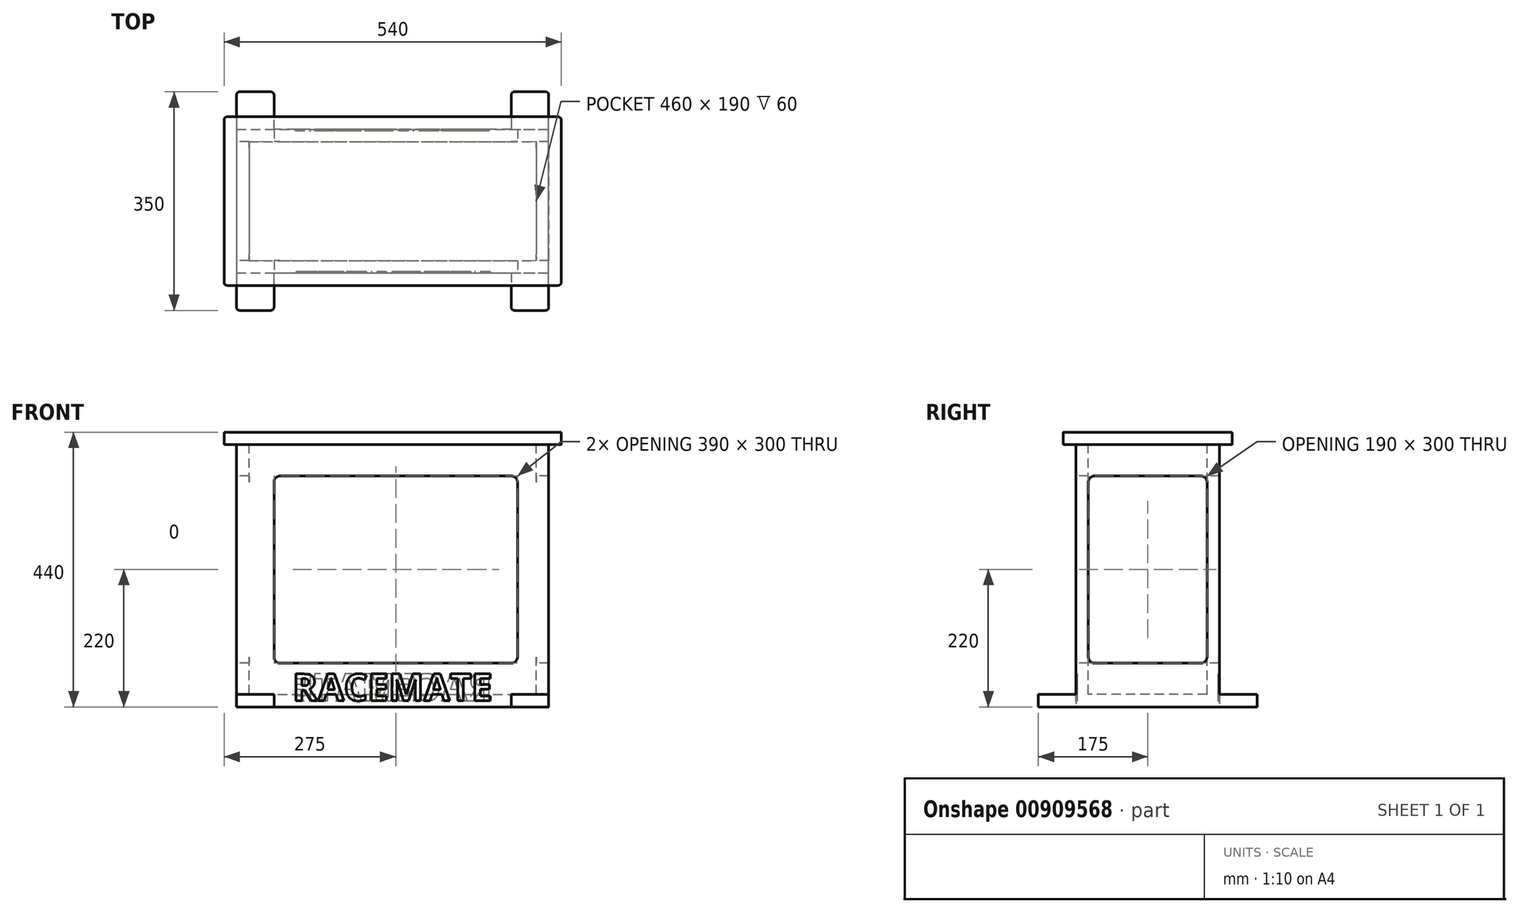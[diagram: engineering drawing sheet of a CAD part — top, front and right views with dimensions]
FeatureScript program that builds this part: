
annotation { "Feature Type Name" : "Feature", "Feature Type Description" : "" }
export const myFeature = defineFeature(function(context is Context, id is Id, definition is map)
    precondition{}
    {
        {
            var Q0;
            Q0=qCreatedBy(makeId("Top.planeOp"),FACE);
            var sketch = newSketch(context, id + "F0", { "sketchPlane" : qUnion([Q0])});
            skLineSegment(sketch, "E0", {"start": v(0, 0) * mm, "end": v(60, 0) * mm});
            skLineSegment(sketch, "E1", {"start": v(60, 0) * mm, "end": v(60, 60) * mm});
            skLineSegment(sketch, "E2", {"start": v(60, 60) * mm, "end": v(440, 60) * mm});
            skLineSegment(sketch, "E3", {"start": v(440, 60) * mm, "end": v(440, 0) * mm});
            skLineSegment(sketch, "E4", {"start": v(440, 0) * mm, "end": v(500, 0) * mm});
            skLineSegment(sketch, "E5", {"start": v(500, 0) * mm, "end": v(500, 350) * mm});
            skLineSegment(sketch, "E6", {"start": v(500, 350) * mm, "end": v(440, 350) * mm});
            skLineSegment(sketch, "E7", {"start": v(440, 350) * mm, "end": v(440, 290) * mm});
            skLineSegment(sketch, "E8", {"start": v(440, 290) * mm, "end": v(60, 290) * mm});
            skLineSegment(sketch, "E9", {"start": v(60, 290) * mm, "end": v(60, 350) * mm});
            skLineSegment(sketch, "E10", {"start": v(60, 350) * mm, "end": v(0, 350) * mm});
            skLineSegment(sketch, "E11", {"start": v(0, 350) * mm, "end": v(0, 0) * mm});
            skSolve(sketch);
        }
        {
            var Q0;
            Q0=makeQuery(id+"F0.imprint","IMPRINT",FACE,{"disambiguationData":[TD([[makeQuery(id+"F0.imprint","IMPRINT",EDGE,{"derivedFrom":sQuery(id+"F0.wireOp",EDGE,"E0")}),1.0]])]});
            var Q1;
            Q1 = qSketchRegion(id + "F2", true);
            extrude(context, id + "F1", {"entities" : qUnion([Q0, Q1]), "depth" : 20 * mm, "offsetDistance" : 25 * mm});
        }
        {
            var Q0;
            Q0=makeQuery(id+"F1.opExtrude","CAP_FACE",FACE,{"disambiguationData":[OSD([sQuery(id+"F0.wireOp",EDGE,"E0"),sQuery(id+"F0.wireOp",EDGE,"E1"),sQuery(id+"F0.wireOp",EDGE,"E2"),sQuery(id+"F0.wireOp",EDGE,"E3"),sQuery(id+"F0.wireOp",EDGE,"E4"),sQuery(id+"F0.wireOp",EDGE,"E5"),sQuery(id+"F0.wireOp",EDGE,"E6"),sQuery(id+"F0.wireOp",EDGE,"E7"),sQuery(id+"F0.wireOp",EDGE,"E8"),sQuery(id+"F0.wireOp",EDGE,"E9"),sQuery(id+"F0.wireOp",EDGE,"E10"),sQuery(id+"F0.wireOp",EDGE,"E11")])],"isStart":false});
            var sketch = newSketch(context, id + "F2", { "sketchPlane" : qUnion([Q0])});
            skLineSegment(sketch, "E12.bottom", {"start": v(0, 290) * mm, "end": v(500, 290) * mm});
            skLineSegment(sketch, "E12.top", {"start": v(0, 60) * mm, "end": v(500, 60) * mm});
            skLineSegment(sketch, "E12.left", {"start": v(0, 290) * mm, "end": v(0, 60) * mm});
            skLineSegment(sketch, "E12.right", {"start": v(500, 290) * mm, "end": v(500, 60) * mm});
            skSolve(sketch);
        }
        {
            var Q0;
            Q0 = qSketchRegion(id + "F2", true);
            var Q1;
            Q1 = qSketchRegion(id + "F4", true);
            extrude(context, id + "F3", {"entities" : qUnion([Q0, Q1]), "operationType" : NewBodyOperationType.ADD, "depth" : 400 * mm, "offsetDistance" : 25 * mm});
        }
        {
            var Q0;
            Q0=makeQuery(id+"F3.opExtrude","CAP_FACE",FACE,{"disambiguationData":[OSD([sQuery(id+"F2.wireOp",EDGE,"E12.bottom"),sQuery(id+"F2.wireOp",EDGE,"E12.top"),sQuery(id+"F2.wireOp",EDGE,"E12.left"),sQuery(id+"F2.wireOp",EDGE,"E12.right")])],"isStart":false});
            var sketch = newSketch(context, id + "F4", { "sketchPlane" : qUnion([Q0])});
            skLineSegment(sketch, "E13.bottom", {"start": v(20, 270) * mm, "end": v(480, 270) * mm});
            skLineSegment(sketch, "E13.top", {"start": v(20, 80) * mm, "end": v(480, 80) * mm});
            skLineSegment(sketch, "E13.left", {"start": v(20, 270) * mm, "end": v(20, 80) * mm});
            skLineSegment(sketch, "E13.right", {"start": v(480, 270) * mm, "end": v(480, 80) * mm});
            skSolve(sketch);
        }
        {
            var Q0;
            Q0 = qSketchRegion(id + "F4", true);
            extrude(context, id + "F5", {"entities" : qUnion([Q0]), "operationType" : NewBodyOperationType.REMOVE, "oppositeDirection" : true, "depth" : 400 * mm, "offsetDistance" : 25 * mm});
        }
        {
            var Q0;
            Q0=makeQuery(id+"F3.boolean.opBoolean","MERGE",FACE,{"derivedFrom":[makeQuery(id+"F1.opExtrude","SWEPT_FACE",FACE,{"disambiguationData":[OSD([sQuery(id+"F0.wireOp",EDGE,"E11")])]}),makeQuery(id+"F3.opExtrude","SWEPT_FACE",FACE,{"disambiguationData":[OSD([sQuery(id+"F2.wireOp",EDGE,"E12.left")])]})]});
            var sketch = newSketch(context, id + "F6", { "sketchPlane" : qUnion([Q0])});
            skLineSegment(sketch, "E14.bottom", {"start": v(-270, 370) * mm, "end": v(-80, 370) * mm});
            skLineSegment(sketch, "E14.top", {"start": v(-270, 70) * mm, "end": v(-80, 70) * mm});
            skLineSegment(sketch, "E14.left", {"start": v(-270, 370) * mm, "end": v(-270, 70) * mm});
            skLineSegment(sketch, "E14.right", {"start": v(-80, 370) * mm, "end": v(-80, 70) * mm});
            skSolve(sketch);
        }
        {
            var Q0;
            Q0 = qSketchRegion(id + "F6", true);
            extrude(context, id + "F7", {"entities" : qUnion([Q0]), "operationType" : NewBodyOperationType.REMOVE, "endBound" : BoundingType.THROUGH_ALL, "oppositeDirection" : true, "depth" : 25 * mm, "offsetDistance" : 25 * mm});
        }
        {
            var Q0;
            Q0=makeQuery(id+"F3.boolean.opBoolean","MERGE",FACE,{"derivedFrom":[makeQuery(id+"F1.opExtrude","SWEPT_FACE",FACE,{"disambiguationData":[OSD([sQuery(id+"F0.wireOp",EDGE,"E2")])]}),makeQuery(id+"F3.opExtrude","SWEPT_FACE",FACE,{"disambiguationData":[OSD([sQuery(id+"F2.wireOp",EDGE,"E12.top")])]})]});
            var sketch = newSketch(context, id + "F8", { "sketchPlane" : qUnion([Q0])});
            skLineSegment(sketch, "E15.bottom", {"start": v(60, 370) * mm, "end": v(450, 370) * mm});
            skLineSegment(sketch, "E15.top", {"start": v(60, 70) * mm, "end": v(450, 70) * mm});
            skLineSegment(sketch, "E15.left", {"start": v(60, 370) * mm, "end": v(60, 70) * mm});
            skLineSegment(sketch, "E15.right", {"start": v(450, 370) * mm, "end": v(450, 70) * mm});
            skSolve(sketch);
        }
        {
            var Q0;
            Q0 = qSketchRegion(id + "F8", true);
            extrude(context, id + "F9", {"entities" : qUnion([Q0]), "operationType" : NewBodyOperationType.REMOVE, "endBound" : BoundingType.THROUGH_ALL, "oppositeDirection" : true, "depth" : 25 * mm, "offsetDistance" : 25 * mm});
        }
        {
            var Q0;
            Q0=makeQuery(id+"F3.opExtrude","CAP_FACE",FACE,{"disambiguationData":[OSD([sQuery(id+"F2.wireOp",EDGE,"E12.bottom"),sQuery(id+"F2.wireOp",EDGE,"E12.top"),sQuery(id+"F2.wireOp",EDGE,"E12.left"),sQuery(id+"F2.wireOp",EDGE,"E12.right")])],"isStart":false});
            var sketch = newSketch(context, id + "F10", { "sketchPlane" : qUnion([Q0])});
            skLineSegment(sketch, "E16", {"start": v(-20, 310) * mm, "end": v(-20, 40) * mm});
            skLineSegment(sketch, "E17", {"start": v(-20, 40) * mm, "end": v(520, 40) * mm});
            skLineSegment(sketch, "E18", {"start": v(520, 40) * mm, "end": v(520, 310) * mm});
            skLineSegment(sketch, "E19", {"start": v(520, 310) * mm, "end": v(-20, 310) * mm});
            skSolve(sketch);
        }
        {
            var Q0;
            Q0 = qSketchRegion(id + "F10", true);
            extrude(context, id + "F11", {"entities" : qUnion([Q0]), "operationType" : NewBodyOperationType.ADD, "surfaceOperationType" : NewSurfaceOperationType.ADD, "depth" : 20 * mm, "offsetDistance" : 25 * mm});
        }
        {
            var Q0;
            Q0=makeQuery(id+"F1.opExtrude","SWEPT_EDGE",EDGE,{"disambiguationData":[OSD([sQuery(id+"F0.wireOp",EDGE,"E0"),sQuery(id+"F0.wireOp",EDGE,"E11")])]});
            var Q1;
            Q1=makeQuery(id+"F1.opExtrude","SWEPT_EDGE",EDGE,{"disambiguationData":[OSD([sQuery(id+"F0.wireOp",EDGE,"E0"),sQuery(id+"F0.wireOp",EDGE,"E1")])]});
            var Q2;
            Q2=makeQuery(id+"F1.opExtrude","SWEPT_EDGE",EDGE,{"disambiguationData":[OSD([sQuery(id+"F0.wireOp",EDGE,"E10"),sQuery(id+"F0.wireOp",EDGE,"E11")])]});
            var Q3;
            Q3=makeQuery(id+"F1.opExtrude","SWEPT_EDGE",EDGE,{"disambiguationData":[OSD([sQuery(id+"F0.wireOp",EDGE,"E4"),sQuery(id+"F0.wireOp",EDGE,"E5")])]});
            var Q4;
            Q4=makeQuery(id+"F1.opExtrude","SWEPT_EDGE",EDGE,{"disambiguationData":[OSD([sQuery(id+"F0.wireOp",EDGE,"E3"),sQuery(id+"F0.wireOp",EDGE,"E4")])]});
            var Q5;
            Q5=makeQuery(id+"F1.opExtrude","SWEPT_EDGE",EDGE,{"disambiguationData":[OSD([sQuery(id+"F0.wireOp",EDGE,"E9"),sQuery(id+"F0.wireOp",EDGE,"E10")])]});
            var Q6;
            Q6=makeQuery(id+"F1.opExtrude","SWEPT_EDGE",EDGE,{"disambiguationData":[OSD([sQuery(id+"F0.wireOp",EDGE,"E5"),sQuery(id+"F0.wireOp",EDGE,"E6")])]});
            var Q7;
            Q7=makeQuery(id+"F1.opExtrude","SWEPT_EDGE",EDGE,{"disambiguationData":[OSD([sQuery(id+"F0.wireOp",EDGE,"E6"),sQuery(id+"F0.wireOp",EDGE,"E7")])]});
            fillet(context, id + "F12", {"entities" : qUnion([Q0, Q1, Q2, Q3, Q4, Q5, Q6, Q7]), "radius" : 5 * mm, "tangentPropagation" : true, "allowEdgeOverflow" : false});
        }
        {
            var Q0;
            Q0=makeQuery(id+"F11.opExtrude","SWEPT_EDGE",EDGE,{"disambiguationData":[OSD([sQuery(id+"F10.wireOp",EDGE,"E18"),sQuery(id+"F10.wireOp",EDGE,"E19")])]});
            var Q1;
            Q1=makeQuery(id+"F11.opExtrude","SWEPT_EDGE",EDGE,{"disambiguationData":[OSD([sQuery(id+"F10.wireOp",EDGE,"E16"),sQuery(id+"F10.wireOp",EDGE,"E19")])]});
            var Q2;
            Q2=makeQuery(id+"F11.opExtrude","SWEPT_EDGE",EDGE,{"disambiguationData":[OSD([sQuery(id+"F10.wireOp",EDGE,"E16"),sQuery(id+"F10.wireOp",EDGE,"E17")])]});
            var Q3;
            Q3=makeQuery(id+"F11.opExtrude","SWEPT_EDGE",EDGE,{"disambiguationData":[OSD([sQuery(id+"F10.wireOp",EDGE,"E17"),sQuery(id+"F10.wireOp",EDGE,"E18")])]});
            fillet(context, id + "F13", {"entities" : qUnion([Q0, Q1, Q2, Q3]), "radius" : 5 * mm, "tangentPropagation" : true, "allowEdgeOverflow" : false});
        }
        {
            var Q0;
            {var subQ0=sQuery(id+"F8.wireOp",EDGE,"E15.top");var subQ1=sQuery(id+"F8.wireOp",EDGE,"E15.left");Q0=makeQuery(id+"F9.boolean.opBoolean","COPY",EDGE,{"disambiguationData":[TD([makeQuery(id+"F1.opExtrude","SWEPT_FACE",FACE,{"disambiguationData":[OSD([sQuery(id+"F0.wireOp",EDGE,"E2")])]})])],"derivedFrom":makeQuery(id+"F9.opExtrude","SWEPT_EDGE",EDGE,{"disambiguationData":[OSD([subQ0,subQ1])]})});}
            var Q1;
            {var subQ0=sQuery(id+"F8.wireOp",EDGE,"E15.top");var subQ1=sQuery(id+"F8.wireOp",EDGE,"E15.left");Q1=makeQuery(id+"F9.boolean.opBoolean","COPY",EDGE,{"disambiguationData":[TD([makeQuery(id+"F1.opExtrude","SWEPT_FACE",FACE,{"disambiguationData":[OSD([sQuery(id+"F0.wireOp",EDGE,"E8")])]})])],"derivedFrom":makeQuery(id+"F9.opExtrude","SWEPT_EDGE",EDGE,{"disambiguationData":[OSD([subQ0,subQ1])]})});}
            var Q2;
            {var subQ0=sQuery(id+"F6.wireOp",EDGE,"E14.top");var subQ1=sQuery(id+"F6.wireOp",EDGE,"E14.left");Q2=makeQuery(id+"F7.boolean.opBoolean","COPY",EDGE,{"disambiguationData":[TD([makeQuery(id+"F1.opExtrude","SWEPT_FACE",FACE,{"disambiguationData":[OSD([sQuery(id+"F0.wireOp",EDGE,"E11")])]})])],"derivedFrom":makeQuery(id+"F7.opExtrude","SWEPT_EDGE",EDGE,{"disambiguationData":[OSD([subQ0,subQ1])]})});}
            var Q3;
            {var subQ0=sQuery(id+"F6.wireOp",EDGE,"E14.top");var subQ1=sQuery(id+"F6.wireOp",EDGE,"E14.left");Q3=makeQuery(id+"F7.boolean.opBoolean","COPY",EDGE,{"disambiguationData":[TD([makeQuery(id+"F1.opExtrude","SWEPT_FACE",FACE,{"disambiguationData":[OSD([sQuery(id+"F0.wireOp",EDGE,"E5")])]})])],"derivedFrom":makeQuery(id+"F7.opExtrude","SWEPT_EDGE",EDGE,{"disambiguationData":[OSD([subQ0,subQ1])]})});}
            var Q4;
            {var subQ0=sQuery(id+"F8.wireOp",EDGE,"E15.top");var subQ1=sQuery(id+"F8.wireOp",EDGE,"E15.right");Q4=makeQuery(id+"F9.boolean.opBoolean","COPY",EDGE,{"disambiguationData":[TD([makeQuery(id+"F1.opExtrude","SWEPT_FACE",FACE,{"disambiguationData":[OSD([sQuery(id+"F0.wireOp",EDGE,"E2")])]})])],"derivedFrom":makeQuery(id+"F9.opExtrude","SWEPT_EDGE",EDGE,{"disambiguationData":[OSD([subQ0,subQ1])]})});}
            var Q5;
            {var subQ0=sQuery(id+"F6.wireOp",EDGE,"E14.top");var subQ1=sQuery(id+"F6.wireOp",EDGE,"E14.right");Q5=makeQuery(id+"F7.boolean.opBoolean","COPY",EDGE,{"disambiguationData":[TD([makeQuery(id+"F1.opExtrude","SWEPT_FACE",FACE,{"disambiguationData":[OSD([sQuery(id+"F0.wireOp",EDGE,"E5")])]})])],"derivedFrom":makeQuery(id+"F7.opExtrude","SWEPT_EDGE",EDGE,{"disambiguationData":[OSD([subQ0,subQ1])]})});}
            var Q6;
            {var subQ0=sQuery(id+"F8.wireOp",EDGE,"E15.top");var subQ1=sQuery(id+"F8.wireOp",EDGE,"E15.right");Q6=makeQuery(id+"F9.boolean.opBoolean","COPY",EDGE,{"disambiguationData":[TD([makeQuery(id+"F1.opExtrude","SWEPT_FACE",FACE,{"disambiguationData":[OSD([sQuery(id+"F0.wireOp",EDGE,"E8")])]})])],"derivedFrom":makeQuery(id+"F9.opExtrude","SWEPT_EDGE",EDGE,{"disambiguationData":[OSD([subQ0,subQ1])]})});}
            var Q7;
            {var subQ0=sQuery(id+"F6.wireOp",EDGE,"E14.top");var subQ1=sQuery(id+"F6.wireOp",EDGE,"E14.right");Q7=makeQuery(id+"F7.boolean.opBoolean","COPY",EDGE,{"disambiguationData":[TD([makeQuery(id+"F1.opExtrude","SWEPT_FACE",FACE,{"disambiguationData":[OSD([sQuery(id+"F0.wireOp",EDGE,"E11")])]})])],"derivedFrom":makeQuery(id+"F7.opExtrude","SWEPT_EDGE",EDGE,{"disambiguationData":[OSD([subQ0,subQ1])]})});}
            var Q8;
            {var subQ0=sQuery(id+"F8.wireOp",EDGE,"E15.bottom");var subQ1=sQuery(id+"F8.wireOp",EDGE,"E15.left");Q8=makeQuery(id+"F9.boolean.opBoolean","COPY",EDGE,{"disambiguationData":[TD([makeQuery(id+"F1.opExtrude","SWEPT_FACE",FACE,{"disambiguationData":[OSD([sQuery(id+"F0.wireOp",EDGE,"E8")])]})])],"derivedFrom":makeQuery(id+"F9.opExtrude","SWEPT_EDGE",EDGE,{"disambiguationData":[OSD([subQ0,subQ1])]})});}
            var Q9;
            {var subQ0=sQuery(id+"F8.wireOp",EDGE,"E15.bottom");var subQ1=sQuery(id+"F8.wireOp",EDGE,"E15.left");Q9=makeQuery(id+"F9.boolean.opBoolean","COPY",EDGE,{"disambiguationData":[TD([makeQuery(id+"F1.opExtrude","SWEPT_FACE",FACE,{"disambiguationData":[OSD([sQuery(id+"F0.wireOp",EDGE,"E2")])]})])],"derivedFrom":makeQuery(id+"F9.opExtrude","SWEPT_EDGE",EDGE,{"disambiguationData":[OSD([subQ0,subQ1])]})});}
            var Q10;
            {var subQ0=sQuery(id+"F6.wireOp",EDGE,"E14.bottom");var subQ1=sQuery(id+"F6.wireOp",EDGE,"E14.right");Q10=makeQuery(id+"F7.boolean.opBoolean","COPY",EDGE,{"disambiguationData":[TD([makeQuery(id+"F1.opExtrude","SWEPT_FACE",FACE,{"disambiguationData":[OSD([sQuery(id+"F0.wireOp",EDGE,"E5")])]})])],"derivedFrom":makeQuery(id+"F7.opExtrude","SWEPT_EDGE",EDGE,{"disambiguationData":[OSD([subQ0,subQ1])]})});}
            var Q11;
            {var subQ0=sQuery(id+"F8.wireOp",EDGE,"E15.bottom");var subQ1=sQuery(id+"F8.wireOp",EDGE,"E15.right");Q11=makeQuery(id+"F9.boolean.opBoolean","COPY",EDGE,{"disambiguationData":[TD([makeQuery(id+"F1.opExtrude","SWEPT_FACE",FACE,{"disambiguationData":[OSD([sQuery(id+"F0.wireOp",EDGE,"E2")])]})])],"derivedFrom":makeQuery(id+"F9.opExtrude","SWEPT_EDGE",EDGE,{"disambiguationData":[OSD([subQ0,subQ1])]})});}
            var Q12;
            {var subQ0=sQuery(id+"F6.wireOp",EDGE,"E14.bottom");var subQ1=sQuery(id+"F6.wireOp",EDGE,"E14.left");Q12=makeQuery(id+"F7.boolean.opBoolean","COPY",EDGE,{"disambiguationData":[TD([makeQuery(id+"F1.opExtrude","SWEPT_FACE",FACE,{"disambiguationData":[OSD([sQuery(id+"F0.wireOp",EDGE,"E5")])]})])],"derivedFrom":makeQuery(id+"F7.opExtrude","SWEPT_EDGE",EDGE,{"disambiguationData":[OSD([subQ0,subQ1])]})});}
            var Q13;
            {var subQ0=sQuery(id+"F8.wireOp",EDGE,"E15.bottom");var subQ1=sQuery(id+"F8.wireOp",EDGE,"E15.right");Q13=makeQuery(id+"F9.boolean.opBoolean","COPY",EDGE,{"disambiguationData":[TD([makeQuery(id+"F1.opExtrude","SWEPT_FACE",FACE,{"disambiguationData":[OSD([sQuery(id+"F0.wireOp",EDGE,"E8")])]})])],"derivedFrom":makeQuery(id+"F9.opExtrude","SWEPT_EDGE",EDGE,{"disambiguationData":[OSD([subQ0,subQ1])]})});}
            var Q14;
            {var subQ0=sQuery(id+"F6.wireOp",EDGE,"E14.bottom");var subQ1=sQuery(id+"F6.wireOp",EDGE,"E14.left");Q14=makeQuery(id+"F7.boolean.opBoolean","COPY",EDGE,{"disambiguationData":[TD([makeQuery(id+"F1.opExtrude","SWEPT_FACE",FACE,{"disambiguationData":[OSD([sQuery(id+"F0.wireOp",EDGE,"E11")])]})])],"derivedFrom":makeQuery(id+"F7.opExtrude","SWEPT_EDGE",EDGE,{"disambiguationData":[OSD([subQ0,subQ1])]})});}
            var Q15;
            {var subQ0=sQuery(id+"F6.wireOp",EDGE,"E14.bottom");var subQ1=sQuery(id+"F6.wireOp",EDGE,"E14.right");Q15=makeQuery(id+"F7.boolean.opBoolean","COPY",EDGE,{"disambiguationData":[TD([makeQuery(id+"F1.opExtrude","SWEPT_FACE",FACE,{"disambiguationData":[OSD([sQuery(id+"F0.wireOp",EDGE,"E11")])]})])],"derivedFrom":makeQuery(id+"F7.opExtrude","SWEPT_EDGE",EDGE,{"disambiguationData":[OSD([subQ0,subQ1])]})});}
            fillet(context, id + "F14", {"entities" : qUnion([Q0, Q1, Q2, Q3, Q4, Q5, Q6, Q7, Q8, Q9, Q10, Q11, Q12, Q13, Q14, Q15]), "radius" : 10 * mm, "tangentPropagation" : true, "allowEdgeOverflow" : false});
        }
        {
            var Q0;
            Q0=makeQuery(id+"F3.boolean.opBoolean","MERGE",FACE,{"derivedFrom":[makeQuery(id+"F1.opExtrude","SWEPT_FACE",FACE,{"disambiguationData":[OSD([sQuery(id+"F0.wireOp",EDGE,"E2")])]}),makeQuery(id+"F3.opExtrude","SWEPT_FACE",FACE,{"disambiguationData":[OSD([sQuery(id+"F2.wireOp",EDGE,"E12.top")])]})]});
            var sketch = newSketch(context, id + "F15", { "sketchPlane" : qUnion([Q0])});
            skText(sketch, "E20", { "text": "RACEMATE\n", "fontName": "OpenSans-Bold.ttf"});
            const initialGuessF15  = {"E20": [0.09, 0.01, 1, 0, 0.0431]};
            skSetInitialGuess(sketch, initialGuessF15);
            skSolve(sketch);
        }
        {
            var Q0;
            Q0=makeQuery(id+"F3.boolean.opBoolean","MERGE",FACE,{"derivedFrom":[makeQuery(id+"F1.opExtrude","SWEPT_FACE",FACE,{"disambiguationData":[OSD([sQuery(id+"F0.wireOp",EDGE,"E8")])]}),makeQuery(id+"F3.opExtrude","SWEPT_FACE",FACE,{"disambiguationData":[OSD([sQuery(id+"F2.wireOp",EDGE,"E12.bottom")])]})]});
            var sketch = newSketch(context, id + "F16", { "sketchPlane" : qUnion([Q0])});
            skText(sketch, "E21", { "text": "RACEMATE", "fontName": "OpenSans-Bold.ttf"});
            const initialGuessF16  = {"E21": [-0.41, 0.01, 1, 0, 0.0431]};
            skSetInitialGuess(sketch, initialGuessF16);
            skSolve(sketch);
        }
        {
            var Q0;
            Q0 = qSketchRegion(id + "F15", true);
            extrude(context, id + "F17", {"entities" : qUnion([Q0]), "operationType" : NewBodyOperationType.REMOVE, "oppositeDirection" : true, "depth" : 2 * mm, "offsetDistance" : 25 * mm});
        }
        {
            var Q0;
            Q0 = qSketchRegion(id + "F16", true);
            extrude(context, id + "F18", {"entities" : qUnion([Q0]), "operationType" : NewBodyOperationType.REMOVE, "oppositeDirection" : true, "depth" : 2 * mm, "offsetDistance" : 25 * mm});
        }
    });
